# Revit family: Вентустановка Naveka Node5 Vertical
name_source: partatom
category: Оборудование
units: mm (PartAtom-declared; Revit-internal decimal feet)

## family parameters
Всегда вертикально = Да
Заголовок OmniClass = Climate Control (HVAC)
На основе рабочей плоскости = Нет
Номер OmniClass = 23.75.00.00
Общий = Нет
При загрузке вырезать с полостями = Нет
Размер круглого соединителя = Использовать диаметр
Тип детали = Нормальный
Точка расчета площади = Нет

## types (10) — shared parameters
ADSK_Единица измерения = шт.
ADSK_Завод-изготовитель = Naveka
ADSK_Наименование = Установка вентиляционная Node5 Compact
ADSK_Примечание = https://progress-nw.ru
Материал = RAL 0000 Серый металл

## per-type parameters (varying)
| type | ADSK_Марка | ADSK_Масса | B | D | D+0.5 | D+4.5 | H | L | Sg | Sv | b | d | l1 | l2 | x2 | Крепления | Мощность вентиляторов, кВт | Мощность калорифера, кВт | Питание, В | Рама | Ток ТЭНа (на фазу), А | Ток вентилятора, А |
| Node5-125/RP-M,VAC,E0.37 | Node5-125/RP-M,VAC,E0.37 Vertical | 57.4 | 350 мм | 62 мм | 62 мм | 66 мм | 640 мм | 726 мм | 152 мм | 81 мм | 125 мм | 125 мм | 134 мм | 135 мм | 555 мм | Да | 0.1 | 0.37 | 1-220 | Нет | 1.7 | 0.5 |
| Node5-160/RP-M,VAC,E1.1 | Node5-160/RP-M,VAC,E1.1 Vertical | 58.2 | 350 мм | 79 мм | 80 мм | 84 мм | 690 мм | 892 мм | 207 мм | 56 мм | 150 мм | 160 мм | 125 мм | 135 мм | 657 мм | Да | 0.17 | 1.1 | 1-220 | Нет | 5.1 | 0.8 |
| Node5-200/RP-M,VAC,E1.5 | Node5-200/RP-M,VAC,E1.5 Vertical | 86.4 | 603 мм | 99 мм | 100 мм | 104 мм | 904 мм | 955 мм | 213 мм | 193 мм | 176 мм | 200 мм | 157 мм | 205 мм | 555 мм | Нет | 0.27 | 1.5 | 1-220 | Да | 6.8 | 1.2 |
| Node5-250/RP-M,VAC,E2.6 | Node5-250/RP-M,VAC,E2.6 Vertical | 87 | 603 мм | 124 мм | 125 мм | 129 мм | 904 мм | 1245 мм | 286 мм | 193 мм | 185 мм | 250 мм | 193 мм | 205 мм | 555 мм | Нет | 0.42 | 2.6 | 1-220 | Да | 11.9 | 1.9 |
| Node5-315/RP-M,VAC,E3.4 | Node5-315/RP-M,VAC,E3.4 Vertical | 89 | 855 мм | 157 мм | 157 мм | 161 мм | 890 мм | 1455 мм | 338 мм | 215 мм | 217 мм | 315 мм | 219 мм | 320 мм | 555 мм | Нет | 0.45 | 3.4 | 3-380 | Да | 5.7 | 2 |
| Node5-125/RP-M,VAC,E0.75 | Node5-125/RP-M,VAC,E0.75 Vertical | 57.4 | 350 мм | 62 мм | 62 мм | 66 мм | 640 мм | 726 мм | 152 мм | 81 мм | 125 мм | 125 мм | 134 мм | 135 мм | 555 мм | Да | 0.1 | 0.75 | 1-220 | Нет | 3.4 | 0.5 |
| Node5-160/RP-M,VAC,E1.5 | Node5-160/RP-M,VAC,E1.5 Vertical | 58.2 | 350 мм | 79 мм | 80 мм | 84 мм | 690 мм | 892 мм | 207 мм | 56 мм | 150 мм | 160 мм | 134 мм | 140 мм | 657 мм | Да | 0.17 | 1.5 | 1-220 | Нет | 6.8 | 0.8 |
| Node5-200/RP-M,VAC,E2.3 | Node5-200/RP-M,VAC,E2.3 Vertical | 86.4 | 603 мм | 99 мм | 100 мм | 104 мм | 904 мм | 955 мм | 213 мм | 193 мм | 176 мм | 200 мм | 157 мм | 205 мм | 555 мм | Нет | 0.27 | 2.3 | 1-220 | Да | 10.2 | 1.2 |
| Node5-250/RP-M,VAC,E3.4 | Node5-250/RP-M,VAC,E3.4 Vertical | 87 | 603 мм | 124 мм | 125 мм | 129 мм | 904 мм | 1245 мм | 286 мм | 193 мм | 185 мм | 250 мм | 193 мм | 205 мм | 555 мм | Нет | 0.42 | 3.4 | 3-380 | Да | 5.7 | 1.9 |
| Node5-315/RP-M,VAC,E4.5 | Node5-315/RP-M,VAC,E4.5 Vertical | 89 | 855 мм | 157 мм | 157 мм | 161 мм | 890 мм | 1455 мм | 338 мм | 215 мм | 217 мм | 315 мм | 219 мм | 320 мм | 555 мм | Нет | 0.45 | 4.5 | 3-380 | Да | 7.6 | 2 |
